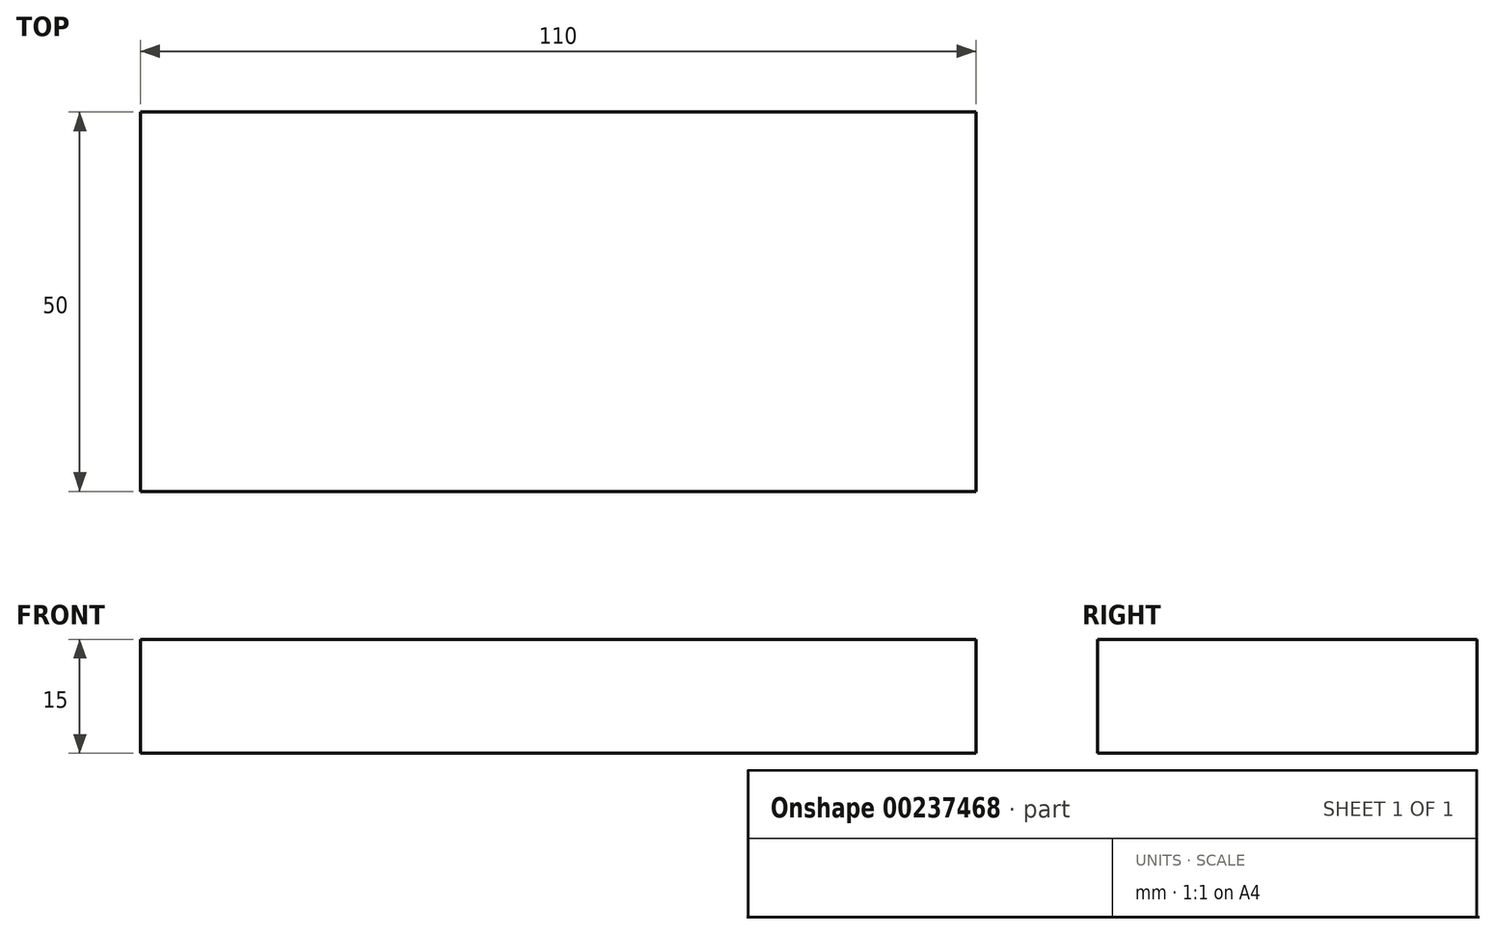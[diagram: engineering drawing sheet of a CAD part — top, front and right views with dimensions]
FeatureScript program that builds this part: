
annotation { "Feature Type Name" : "Feature", "Feature Type Description" : "" }
export const myFeature = defineFeature(function(context is Context, id is Id, definition is map)
    precondition{}
    {
        {
            var Q0;
            Q0=qCreatedBy(makeId("Top.planeOp"),FACE);
            var sketch = newSketch(context, id + "F0", { "sketchPlane" : qUnion([Q0])});
            skLineSegment(sketch, "E0.bottom", {"start": v(55, 25) * mm, "end": v(-55, 25) * mm});
            skLineSegment(sketch, "E0.top", {"start": v(55, -25) * mm, "end": v(-55, -25) * mm});
            skLineSegment(sketch, "E0.left", {"start": v(55, 25) * mm, "end": v(55, -25) * mm});
            skLineSegment(sketch, "E0.right", {"start": v(-55, 25) * mm, "end": v(-55, -25) * mm});
            skPoint(sketch, "E0.middle", {"position": v(0, 0) * mm});
            skSolve(sketch);
        }
        {
            var Q0;
            Q0 = qSketchRegion(id + "F0", true);
            extrude(context, id + "F1", {"entities" : qUnion([Q0]), "depth" : 15 * mm});
        }
    });
